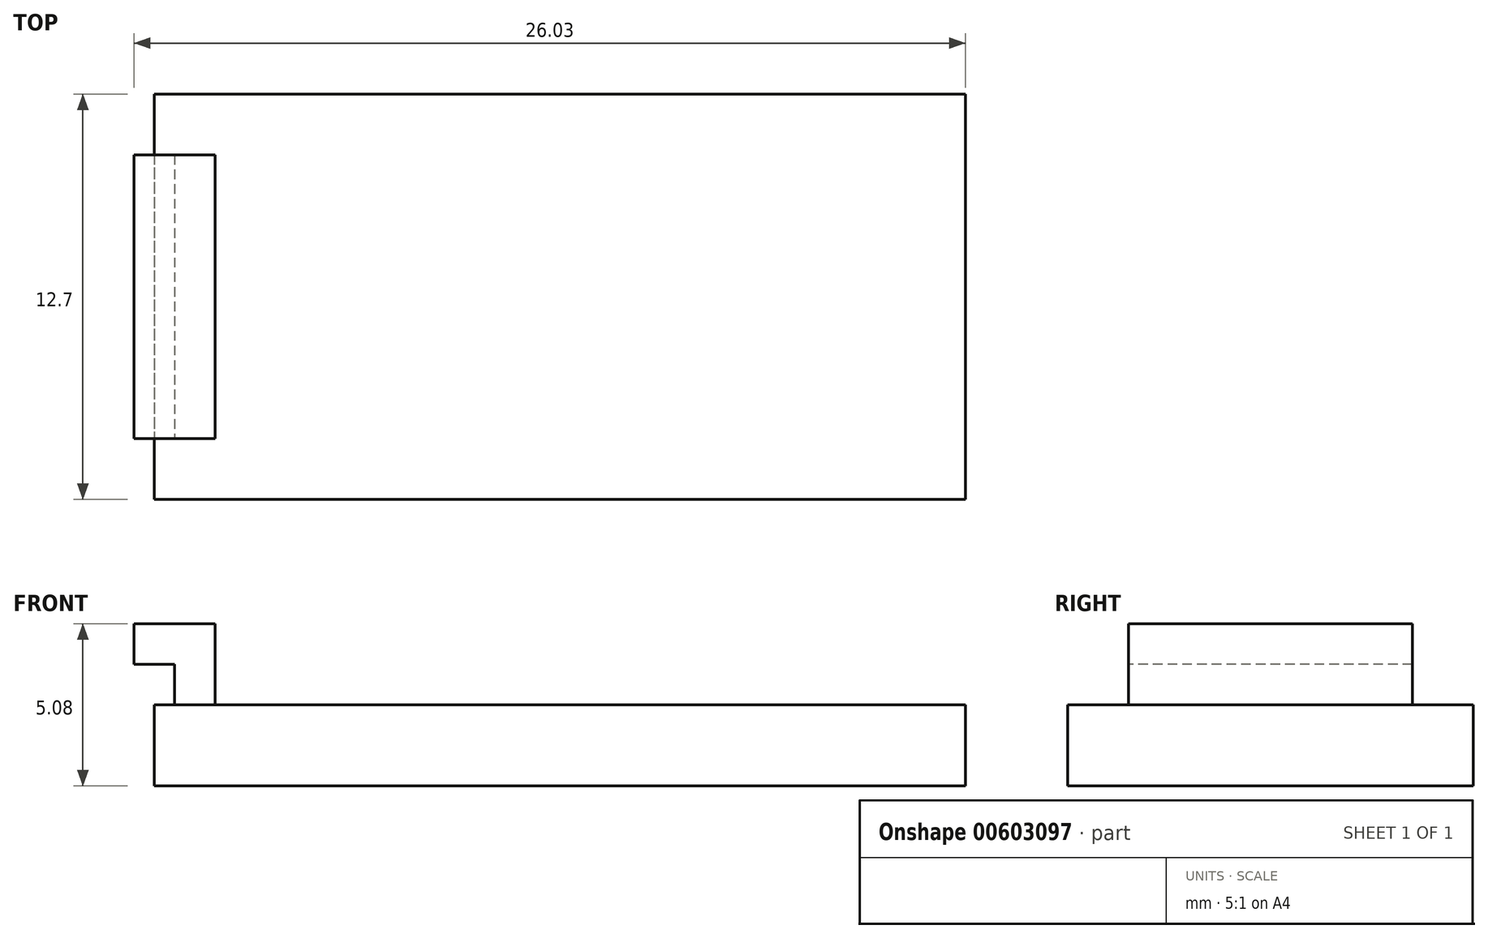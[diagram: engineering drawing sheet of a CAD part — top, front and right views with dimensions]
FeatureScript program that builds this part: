
annotation { "Feature Type Name" : "Feature", "Feature Type Description" : "" }
export const myFeature = defineFeature(function(context is Context, id is Id, definition is map)
    precondition{}
    {
        {
            var Q0;
            Q0=qCreatedBy(makeId("Top.planeOp"),FACE);
            var sketch = newSketch(context, id + "F0", { "sketchPlane" : qUnion([Q0])});
            skLineSegment(sketch, "E0.bottom", {"start": v(12.7, 6.35) * mm, "end": v(-12.7, 6.35) * mm});
            skLineSegment(sketch, "E0.top", {"start": v(12.7, -6.35) * mm, "end": v(-12.7, -6.35) * mm});
            skLineSegment(sketch, "E0.left", {"start": v(12.7, 6.35) * mm, "end": v(12.7, -6.35) * mm});
            skLineSegment(sketch, "E0.right", {"start": v(-12.7, 6.35) * mm, "end": v(-12.7, -6.35) * mm});
            skPoint(sketch, "E0.middle", {"position": v(0, 0) * mm});
            skSolve(sketch);
        }
        {
            var Q0;
            Q0 = qSketchRegion(id + "F0", true);
            extrude(context, id + "F1", {"entities" : qUnion([Q0]), "depth" : 2.54 * mm, "offsetDistance" : 25.4 * mm});
        }
        {
            var Q0;
            Q0=makeQuery(id+"F1.opExtrude","CAP_FACE",FACE,{"disambiguationData":[OSD([sQuery(id+"F0.wireOp",EDGE,"E0.bottom"),sQuery(id+"F0.wireOp",EDGE,"E0.top"),sQuery(id+"F0.wireOp",EDGE,"E0.left"),sQuery(id+"F0.wireOp",EDGE,"E0.right")])],"isStart":false});
            var sketch = newSketch(context, id + "F2", { "sketchPlane" : qUnion([Q0])});
            skLineSegment(sketch, "E1.bottom", {"start": v(-10.8, 4.44) * mm, "end": v(-12.07, 4.44) * mm});
            skLineSegment(sketch, "E1.top", {"start": v(-10.8, -4.45) * mm, "end": v(-12.07, -4.45) * mm});
            skLineSegment(sketch, "E1.left", {"start": v(-10.8, 4.44) * mm, "end": v(-10.8, -4.45) * mm});
            skLineSegment(sketch, "E1.right", {"start": v(-12.07, 4.44) * mm, "end": v(-12.07, -4.45) * mm});
            skPoint(sketch, "E1.middle", {"position": v(-11.43, 0) * mm});
            skPoint(sketch, "E1.middle.positionSnap0", {"position": v(-12.7, 0) * mm});
            skPoint(sketch, "E1.centerSnap0", {"position": v(-12.7, 0) * mm});
            skSolve(sketch);
        }
        {
            var Q0;
            Q0 = qSketchRegion(id + "F2", true);
            extrude(context, id + "F3", {"entities" : qUnion([Q0]), "operationType" : NewBodyOperationType.ADD, "depth" : 2.54 * mm, "offsetDistance" : 25.4 * mm});
        }
        {
            var Q0;
            Q0=makeQuery(id+"F3.opExtrude","SWEPT_FACE",FACE,{"disambiguationData":[OSD([sQuery(id+"F2.wireOp",EDGE,"E1.right")])]});
            var sketch = newSketch(context, id + "F4", { "sketchPlane" : qUnion([Q0])});
            skLineSegment(sketch, "E2.bottom", {"start": v(-4.44, 5.08) * mm, "end": v(4.45, 5.08) * mm});
            skLineSegment(sketch, "E2.top", {"start": v(-4.44, 3.81) * mm, "end": v(4.45, 3.81) * mm});
            skLineSegment(sketch, "E2.left", {"start": v(-4.44, 5.08) * mm, "end": v(-4.44, 3.81) * mm});
            skLineSegment(sketch, "E2.right", {"start": v(4.45, 5.08) * mm, "end": v(4.45, 3.81) * mm});
            skSolve(sketch);
        }
        {
            var Q0;
            Q0 = qSketchRegion(id + "F4", true);
            extrude(context, id + "F5", {"entities" : qUnion([Q0]), "operationType" : NewBodyOperationType.ADD, "depth" : 1.27 * mm, "offsetDistance" : 25.4 * mm});
        }
    });
